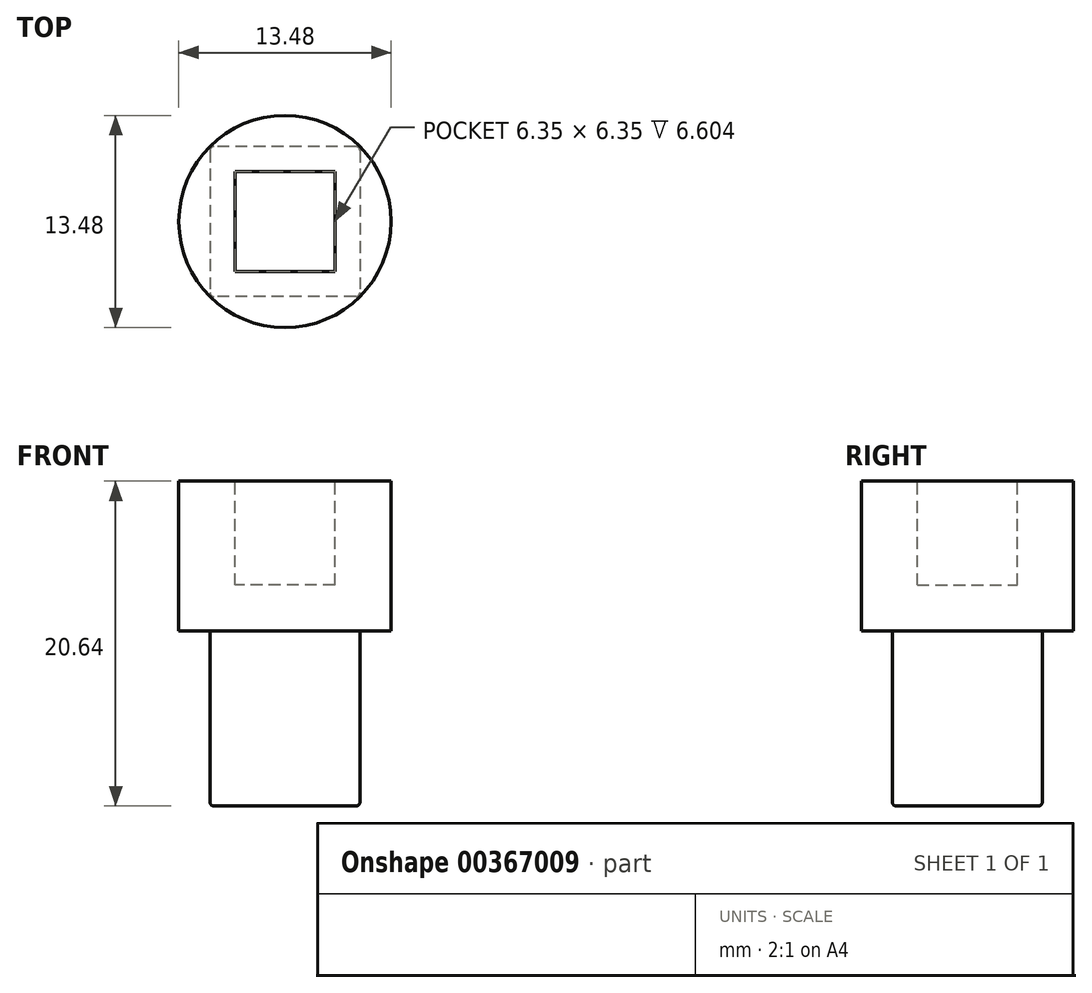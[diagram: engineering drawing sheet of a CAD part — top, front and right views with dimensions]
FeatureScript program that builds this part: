
annotation { "Feature Type Name" : "Feature", "Feature Type Description" : "" }
export const myFeature = defineFeature(function(context is Context, id is Id, definition is map)
    precondition{}
    {
        {
            var Q0;
            Q0=qCreatedBy(makeId("Top.planeOp"),FACE);
            var sketch = newSketch(context, id + "F0", { "sketchPlane" : qUnion([Q0])});
            skLineSegment(sketch, "E0.bottom", {"start": v(4.5, 4.76) * mm, "end": v(-4.5, 4.76) * mm});
            skLineSegment(sketch, "E0.top", {"start": v(4.5, -4.76) * mm, "end": v(-4.5, -4.76) * mm});
            skLineSegment(sketch, "E0.left", {"start": v(4.76, 4.5) * mm, "end": v(4.76, -4.5) * mm});
            skLineSegment(sketch, "E0.right", {"start": v(-4.76, 4.5) * mm, "end": v(-4.76, -4.5) * mm});
            skPoint(sketch, "E0.middle", {"position": v(0, 0) * mm});
            skPoint(sketch, "E1.visualSharp", {"position": v(-4.76, 4.76) * mm});
            skArc(sketch, "E1.filletArc", {"start": v(-4.5, 4.76) * mm, "mid": v(-4.69, 4.69) * mm, "end": v(-4.76, 4.5) * mm});
            skPoint(sketch, "E2.visualSharp", {"position": v(4.76, 4.76) * mm});
            skArc(sketch, "E2.filletArc", {"start": v(4.76, 4.5) * mm, "mid": v(4.69, 4.69) * mm, "end": v(4.5, 4.76) * mm});
            skPoint(sketch, "E3.visualSharp", {"position": v(4.76, -4.76) * mm});
            skArc(sketch, "E3.filletArc", {"start": v(4.5, -4.76) * mm, "mid": v(4.69, -4.69) * mm, "end": v(4.76, -4.5) * mm});
            skPoint(sketch, "E4.visualSharp", {"position": v(-4.76, -4.76) * mm});
            skArc(sketch, "E4.filletArc", {"start": v(-4.76, -4.5) * mm, "mid": v(-4.69, -4.69) * mm, "end": v(-4.5, -4.76) * mm});
            skSolve(sketch);
        }
        {
            var Q0;
            Q0 = qSketchRegion(id + "F0", true);
            extrude(context, id + "F1", {"entities" : qUnion([Q0]), "depth" : 11.1 * mm});
        }
        {
            var Q0;
            Q0=makeQuery(id+"F1.opExtrude","CAP_EDGE",EDGE,{"disambiguationData":[OSD([sQuery(id+"F0.wireOp",EDGE,"E0.left")])],"isStart":true});
            fillet(context, id + "F2", {"entities" : qUnion([Q0]), "radius" : 0.25 * mm, "tangentPropagation" : true, "allowEdgeOverflow" : false});
        }
        {
            var Q0;
            Q0=makeQuery(id+"F1.opExtrude","CAP_FACE",FACE,{"disambiguationData":[OSD([sQuery(id+"F0.wireOp",EDGE,"E0.bottom"),sQuery(id+"F0.wireOp",EDGE,"E0.top"),sQuery(id+"F0.wireOp",EDGE,"E0.left"),sQuery(id+"F0.wireOp",EDGE,"E0.right"),sQuery(id+"F0.wireOp",EDGE,"E1.filletArc"),sQuery(id+"F0.wireOp",EDGE,"E2.filletArc"),sQuery(id+"F0.wireOp",EDGE,"E3.filletArc"),sQuery(id+"F0.wireOp",EDGE,"E4.filletArc")])],"isStart":false});
            var sketch = newSketch(context, id + "F3", { "sketchPlane" : qUnion([Q0])});
            skCircle(sketch, "E5", {"center": v(0, 0) * mm, "radius": 6.74 * mm});
            skSolve(sketch);
        }
        {
            var Q0;
            Q0 = qSketchRegion(id + "F3", true);
            extrude(context, id + "F4", {"entities" : qUnion([Q0]), "operationType" : NewBodyOperationType.ADD, "depth" : 9.52 * mm});
        }
        {
            var Q0;
            Q0=makeQuery(id+"F4.opExtrude","CAP_FACE",FACE,{"disambiguationData":[OSD([sQuery(id+"F3.wireOp",EDGE,"E5")])],"isStart":false});
            var sketch = newSketch(context, id + "F5", { "sketchPlane" : qUnion([Q0])});
            skLineSegment(sketch, "E6.bottom", {"start": v(3.18, -3.18) * mm, "end": v(-3.18, -3.18) * mm});
            skLineSegment(sketch, "E6.top", {"start": v(3.17, 3.17) * mm, "end": v(-3.17, 3.17) * mm});
            skLineSegment(sketch, "E6.left", {"start": v(3.18, -3.18) * mm, "end": v(3.18, 3.17) * mm});
            skLineSegment(sketch, "E6.right", {"start": v(-3.18, -3.18) * mm, "end": v(-3.18, 3.17) * mm});
            skPoint(sketch, "E6.middle", {"position": v(0, 0) * mm});
            skSolve(sketch);
        }
        {
            var Q0;
            Q0 = qSketchRegion(id + "F5", true);
            extrude(context, id + "F6", {"entities" : qUnion([Q0]), "operationType" : NewBodyOperationType.REMOVE, "oppositeDirection" : true, "depth" : 6.6 * mm});
        }
    });
